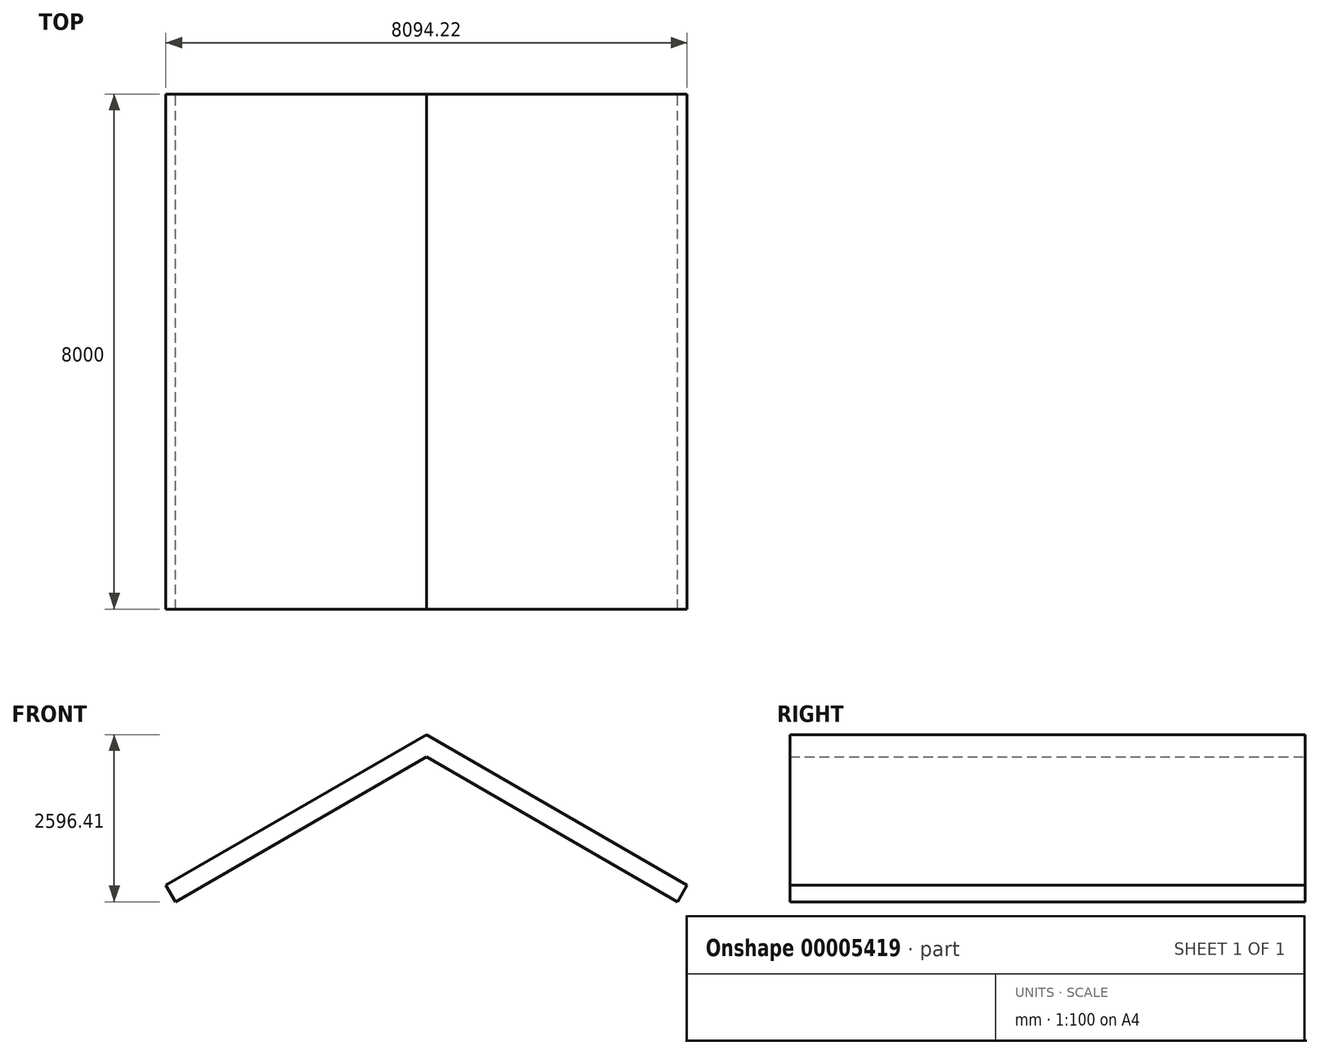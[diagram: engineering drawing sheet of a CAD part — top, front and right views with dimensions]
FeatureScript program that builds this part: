
annotation { "Feature Type Name" : "Feature", "Feature Type Description" : "" }
export const myFeature = defineFeature(function(context is Context, id is Id, definition is map)
    precondition{}
    {
        {
            var Q0;
            Q0=qCreatedBy(makeId("Front.planeOp"),FACE);
            var sketch = newSketch(context, id + "F0", { "sketchPlane" : qUnion([Q0])});
            skLineSegment(sketch, "E0", {"start": v(-4047.11, 0) * mm, "end": v(0, 2336.6) * mm});
            skLineSegment(sketch, "E1", {"start": v(0, 2336.6) * mm, "end": v(0, 1990.2) * mm});
            skLineSegment(sketch, "E2", {"start": v(0, 1990.2) * mm, "end": v(-3897.11, -259.8) * mm});
            skLineSegment(sketch, "E3", {"start": v(-3897.11, -259.8) * mm, "end": v(-4047.11, 0) * mm});
            skLineSegment(sketch, "E4.0.MirrorCS", {"start": v(4047.11, 0) * mm, "end": v(0, 2336.6) * mm});
            skLineSegment(sketch, "E5.0.MirrorCS", {"start": v(3897.11, -259.8) * mm, "end": v(4047.11, 0) * mm});
            skLineSegment(sketch, "E6.0.MirrorCS", {"start": v(0, 1990.2) * mm, "end": v(3897.11, -259.8) * mm});
            skSolve(sketch);
        }
        {
            var Q0;
            Q0=makeQuery(id+"F0.imprint","IMPRINT",FACE,{"disambiguationData":[TD([[makeQuery(id+"F0.imprint","IMPRINT",EDGE,{"derivedFrom":sQuery(id+"F0.wireOp",EDGE,"E0")}),-1.0]])]});
            var Q1;
            Q1=makeQuery(id+"F0.imprint","IMPRINT",FACE,{"disambiguationData":[TD([[makeQuery(id+"F0.imprint","IMPRINT",EDGE,{"derivedFrom":sQuery(id+"F0.wireOp",EDGE,"E1")}),1.0]])]});
            extrude(context, id + "F1", {"entities" : qUnion([Q0, Q1]), "depth" : 8000 * mm});
        }
    });
